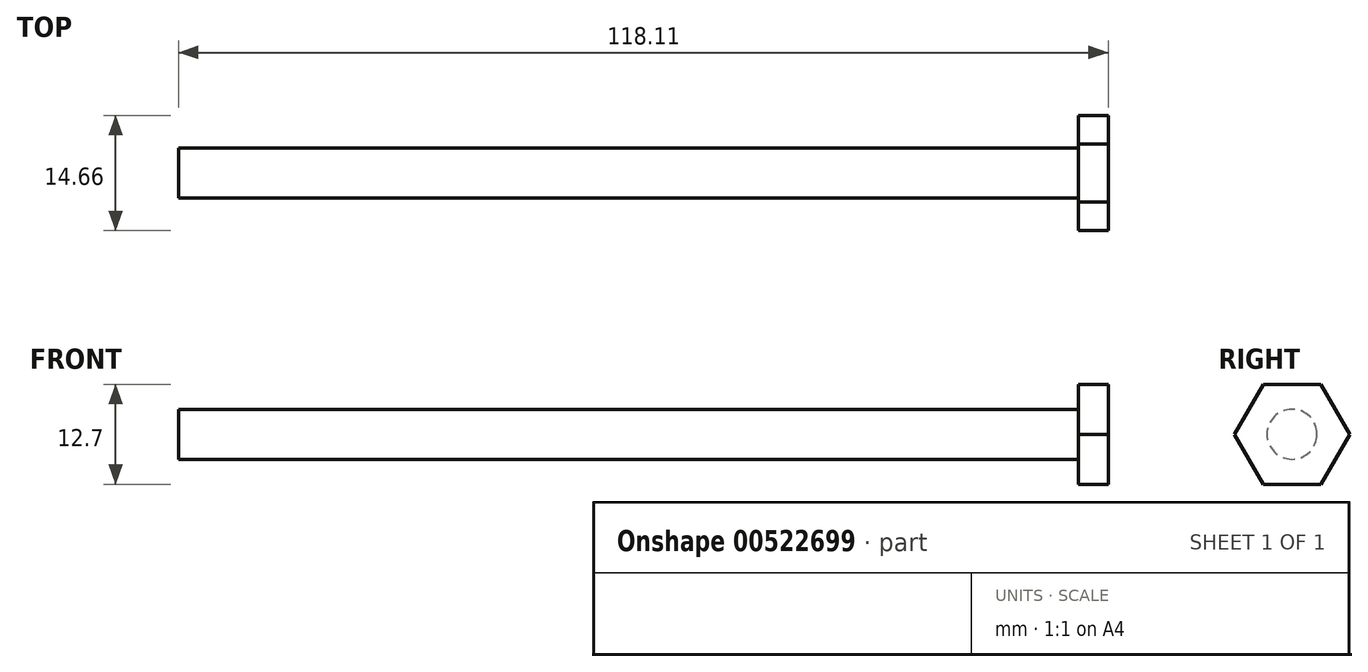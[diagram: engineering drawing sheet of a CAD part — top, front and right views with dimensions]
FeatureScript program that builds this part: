
annotation { "Feature Type Name" : "Feature", "Feature Type Description" : "" }
export const myFeature = defineFeature(function(context is Context, id is Id, definition is map)
    precondition{}
    {
        {
            var Q0;
            Q0=qCreatedBy(makeId("Right.planeOp"),FACE);
            var sketch = newSketch(context, id + "F0", { "sketchPlane" : qUnion([Q0])});
            skCircle(sketch, "E0.cCircle", {"center": v(0, 0) * mm, "radius": 6.35 * mm, "construction": true});
            skLineSegment(sketch, "E0.0", {"start": v(3.67, -6.35) * mm, "end": v(-3.67, -6.35) * mm});
            skLineSegment(sketch, "E0.1", {"start": v(-3.67, -6.35) * mm, "end": v(-7.33, 0) * mm});
            skLineSegment(sketch, "E0.2", {"start": v(-7.33, 0) * mm, "end": v(-3.67, 6.35) * mm});
            skLineSegment(sketch, "E0.3", {"start": v(-3.67, 6.35) * mm, "end": v(3.67, 6.35) * mm});
            skLineSegment(sketch, "E0.4", {"start": v(3.67, 6.35) * mm, "end": v(7.33, 0) * mm});
            skLineSegment(sketch, "E0.5", {"start": v(7.33, 0) * mm, "end": v(3.67, -6.35) * mm});
            skPoint(sketch, "E0.0.midPoint", {"position": v(0, -6.35) * mm});
            skSolve(sketch);
        }
        {
            var Q0;
            Q0 = qSketchRegion(id + "F0", true);
            extrude(context, id + "F1", {"entities" : qUnion([Q0]), "depth" : 3.8 * mm, "offsetDistance" : 25.4 * mm});
        }
        {
            var Q0;
            Q0=qCreatedBy(makeId("Right.planeOp"),FACE);
            var sketch = newSketch(context, id + "F2", { "sketchPlane" : qUnion([Q0])});
            skCircle(sketch, "E1", {"center": v(0, 0) * mm, "radius": 3.18 * mm});
            skSolve(sketch);
        }
        {
            var Q0;
            Q0 = qSketchRegion(id + "F2", true);
            extrude(context, id + "F3", {"entities" : qUnion([Q0]), "operationType" : NewBodyOperationType.ADD, "oppositeDirection" : true, "depth" : 114.3 * mm, "offsetDistance" : 25.4 * mm});
        }
    });
